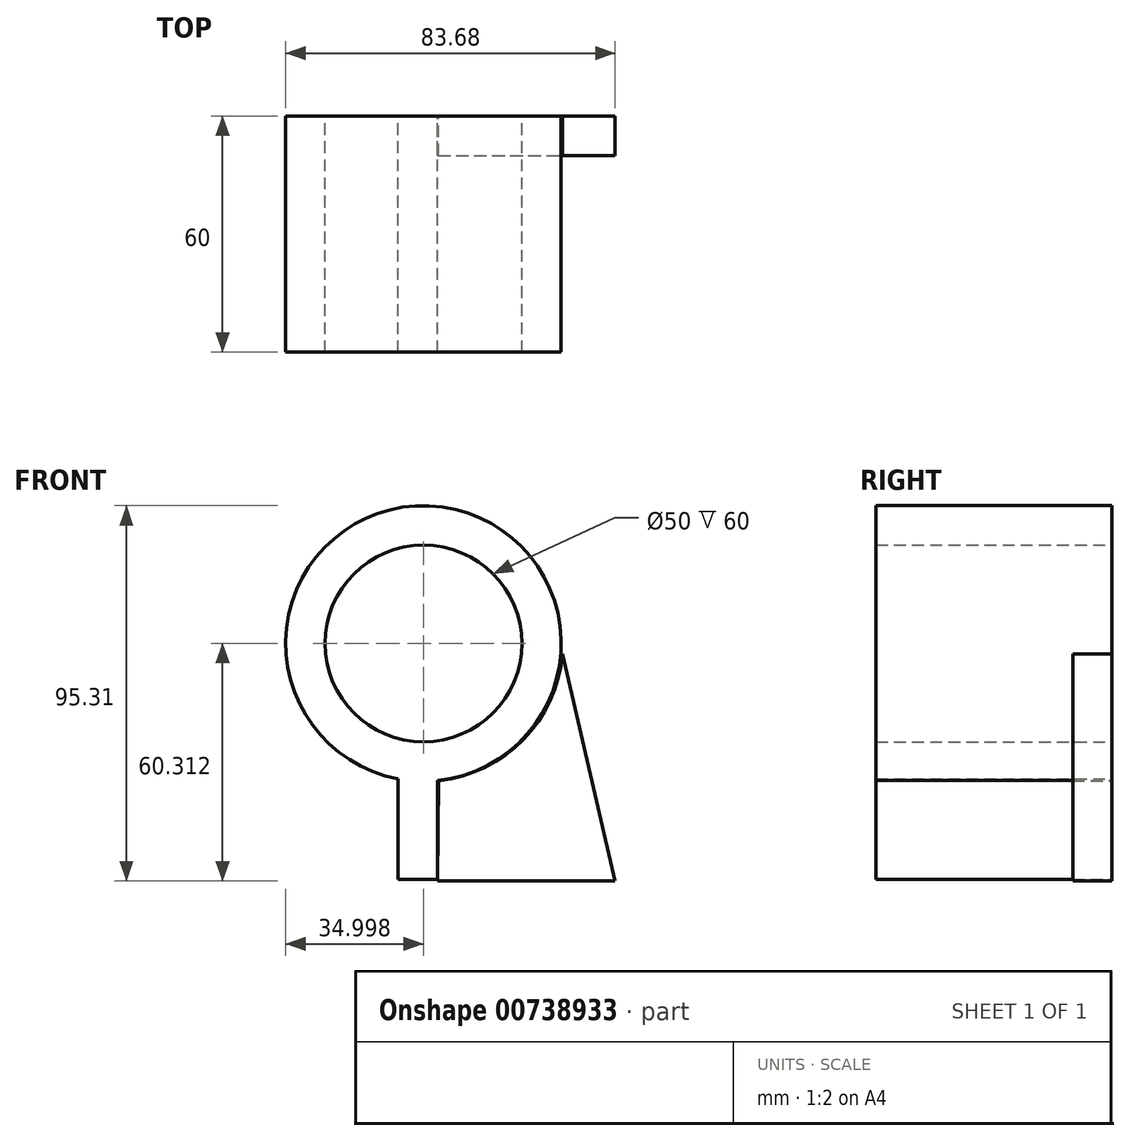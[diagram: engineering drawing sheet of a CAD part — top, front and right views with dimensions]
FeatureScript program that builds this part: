
annotation { "Feature Type Name" : "Feature", "Feature Type Description" : "" }
export const myFeature = defineFeature(function(context is Context, id is Id, definition is map)
    precondition{}
    {
        {
            var Q0;
            Q0=qCreatedBy(makeId("Front.planeOp"),FACE);
            var sketch = newSketch(context, id + "F0", { "sketchPlane" : qUnion([Q0])});
            skCircle(sketch, "E0", {"center": v(-26.18, 14.63) * mm, "radius": 25 * mm});
            skCircle(sketch, "E1", {"center": v(-26.18, 14.63) * mm, "radius": 35 * mm});
            skLineSegment(sketch, "E2", {"start": v(-22.58, -20.18) * mm, "end": v(-22.58, -45.37) * mm});
            skLineSegment(sketch, "E3", {"start": v(-22.58, -45.37) * mm, "end": v(-32.67, -45.37) * mm});
            skLineSegment(sketch, "E4", {"start": v(-32.67, -45.37) * mm, "end": v(-32.67, -19.76) * mm});
            skSolve(sketch);
        }
        {
            var Q0;
            Q0=qSketchRegion(id+"F0",true);
            extrude(context, id + "F1", {"entities" : qUnion([Q0]), "depth" : 60 * mm, "offsetDistance" : 25 * mm});
        }
        {
            var Q0;
            Q0=qCreatedBy(makeId("Front.planeOp"),FACE);
            var sketch = newSketch(context, id + "F2", { "sketchPlane" : qUnion([Q0])});
            skLineSegment(sketch, "E5", {"start": v(-22.56, -45.68) * mm, "end": v(22.5, -45.68) * mm});
            skLineSegment(sketch, "E6", {"start": v(22.5, -45.68) * mm, "end": v(9.14, 11.96) * mm});
            skArc(sketch, "E7", {"start": v(-22.3, -20.27) * mm, "mid": v(-0.8, -9.8) * mm, "end": v(9.14, 11.96) * mm});
            skLineSegment(sketch, "E8", {"start": v(-22.56, -45.68) * mm, "end": v(-22.3, -20.27) * mm});
            skSolve(sketch);
        }
        {
            var Q0;
            Q0=makeQuery(id+"F2.imprint","IMPRINT",FACE,{"disambiguationData":[TD([[makeQuery(id+"F2.imprint","IMPRINT",EDGE,{"derivedFrom":sQuery(id+"F2.wireOp",EDGE,"E5")}),1.0]])]});
            extrude(context, id + "F3", {"entities" : qUnion([Q0]), "depth" : 10 * mm, "offsetDistance" : 25 * mm});
        }
    });
